# Revit family: Comfort_Window_I_Top_Hung_Standard
name_source: partatom
category: Windows
revit_build: Autodesk Revit 2014 (Build: 20130308_1515(x64)
units: mm (PartAtom-declared; Revit-internal decimal feet)

## types (8) — shared parameters
DG Gasket Thickness = 12 mm  [stored 0.0393701 ft]
Description = Comfort Window, Top Hung, Type I
Double Glazing Gasket Finish = Double Glazing Gasket Material
Frame Depth = 33 mm  [stored 0.108268 ft]
Frame Edge Thickness = 26 mm
Limit Fixed Pane Height Max = 1800 mm  [stored 5.90551 ft]
Limit Fixed Pane Height Min = 200 mm  [stored 0.656168 ft]
Limit Fixed Pane Width Max = 1800 mm  [stored 5.90551 ft]
Limit Fixed Pane Width Min = 200 mm  [stored 0.656168 ft]
Limit Sash Height Max = 750 mm  [stored 2.46063 ft]
Limit Sash Height Min = 300 mm  [stored 0.984252 ft]
Limit Sash Width Max = 1200 mm
Limit Sash Width Min = 300 mm  [stored 0.984252 ft]
Limit Window Height Max = 1852 mm
Manufacturer = Crealco
Max System DG One Piece Thickness = 4 mm  [stored 0.0131234 ft]
Max System DG Unit Thickness = 20 mm  [stored 0.0656168 ft]
Model = Comfort Window
Mullion Width = 27 mm  [stored 0.0885827 ft]
Rough Height = 590 mm  [stored 1.9357 ft]
Rough Width = 902 mm  [stored 2.95932 ft]
Sash Frame Gap = 5 mm  [stored 0.0164042 ft]
Sash Frame Side Gap = 12 mm  [stored 0.0393701 ft]
Sash Side Gap = 38 mm
Set Sash Height = 515 mm  [stored 1.68963 ft]
Set Sash Width = 515 mm  [stored 1.68963 ft]
Transom Height = 27 mm  [stored 0.0885827 ft]
URL = http://www.crealco.co.za
zero-valued in all types: Visual Light Transmittance

## per-type parameters (varying)
| type | Clearvue SHGC Value | Clearvue U Value | Energy Advantage SHGC Value | Energy Advantage U Value | Intruderprufe LowE SHGC Value | Intruderprufe LowE U Value | Intruderprufe SHGC Value | Intruderprufe U Value | SmartGlass Elite SHGC Value | SmartGlass Elite U Value | SmartGlass Plus SHGC Value | SmartGlass Plus U Value | SmartGlass Standard SHGC Value | SmartGlass Standard U Value | SmartGlass Superior SHGC Value | SmartGlass Superior U Value | Window Height | Window Width |
| Comfort-1215DT | 0.604 | 6.09 | 0.541 | 4.66 | 0.512 | 4.54 | 0.574 | 5.99 | 0.295 | 3.29 | 0.402 | 3.44 | 0.539 | 3.97 | 0.257 | 3.29 | 1490 mm  [stored 4.88845 ft] | 1190 mm  [stored 3.9042 ft] |
| Comfort-1515DT | 0.643 | 6.06 | 0.576 | 4.5 | 0.543 | 4.39 | 0.61 | 5.95 | 0.312 | 3.03 | 0.425 | 3.19 | 0.572 | 3.77 | 0.271 | 3.03 | 1490 mm  [stored 4.88845 ft] | 1490 mm  [stored 4.88845 ft] |
| Comfort-1218DT | 0.624 | 6.07 | 0.56 | 4.58 | 0.529 | 4.46 | 0.593 | 5.97 | 0.304 | 3.16 | 0.414 | 3.31 | 0.556 | 3.87 | 0.265 | 3.16 | 1790 mm  [stored 5.8727 ft] | 1190 mm  [stored 3.9042 ft] |
| Comfort-1518DT | 0.661 | 6.04 | 0.592 | 4.44 | 0.557 | 4.33 | 0.627 | 5.93 | 0.319 | 2.91 | 0.436 | 3.08 | 0.587 | 3.69 | 0.278 | 2.92 | 1790 mm  [stored 5.8727 ft] | 1490 mm  [stored 4.88845 ft] |
| Comfort-1815DT | 0.645 | 6.05 | 0.578 | 4.5 | 0.545 | 4.38 | 0.612 | 5.95 | 0.313 | 3.02 | 0.427 | 3.18 | 0.574 | 3.77 | 0.272 | 3.02 | 1490 mm  [stored 4.88845 ft] | 1790 mm  [stored 5.8727 ft] |
| Comfort-1818DT | 0.666 | 6.04 | 0.596 | 4.42 | 0.561 | 4.31 | 0.631 | 5.93 | 0.321 | 2.89 | 0.439 | 3.05 | 0.591 | 3.67 | 0.279 | 2.89 | 1790 mm  [stored 5.8727 ft] | 1790 mm  [stored 5.8727 ft] |
| Comfort-2415DT | 0.667 | 6.03 | 0.597 | 4.41 | 0.562 | 4.3 | 0.632 | 5.93 | 0.322 | 2.87 | 0.44 | 3.04 | 0.592 | 3.66 | 0.28 | 2.88 | 1490 mm  [stored 4.88845 ft] | 2390 mm  [stored 7.84121 ft] |
| Comfort-2418DT | 0.686 | 6.02 | 0.614 | 4.34 | 0.577 | 4.23 | 0.65 | 5.91 | 0.33 | 2.75 | 0.452 | 2.93 | 0.608 | 3.56 | 0.287 | 2.76 | 1790 mm  [stored 5.8727 ft] | 2390 mm  [stored 7.84121 ft] |

note: [stored X ft] marks values corroborated as IEEE doubles in the binary element streams (Revit-internal decimal feet)

## geometry (parser evidence)
native form markers: Sweep x18
no freeform markers — native parametric forms only
